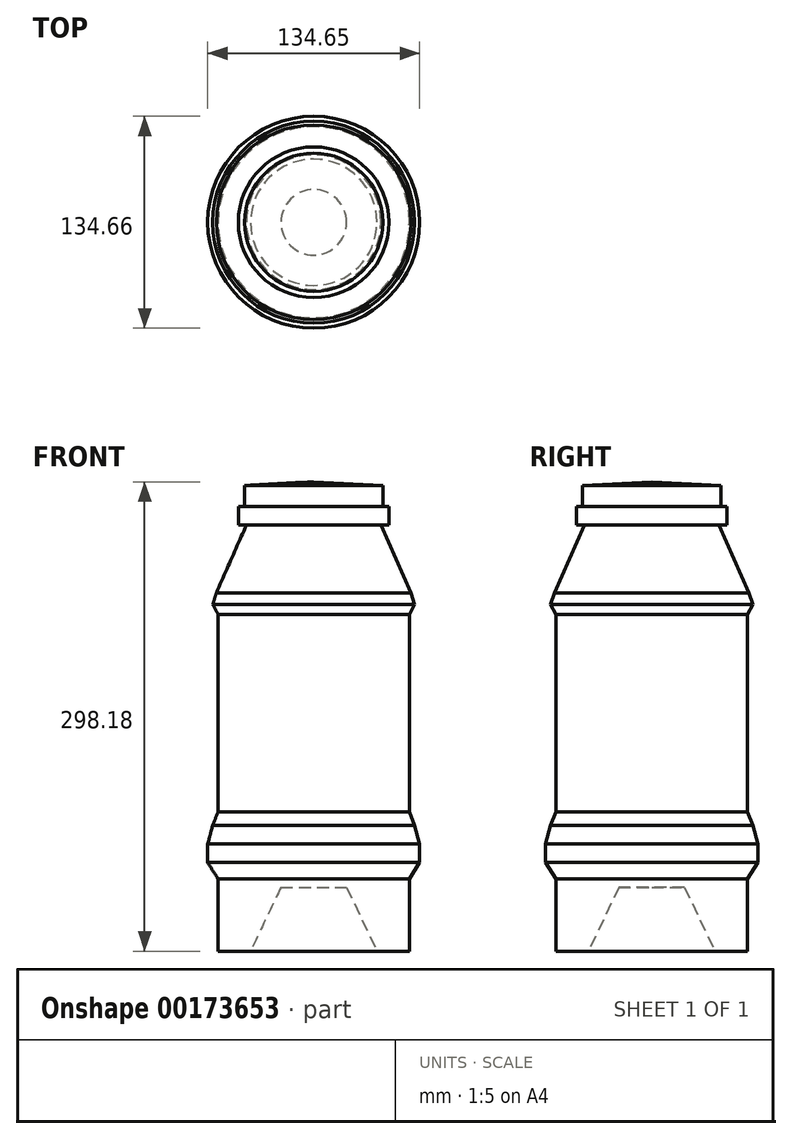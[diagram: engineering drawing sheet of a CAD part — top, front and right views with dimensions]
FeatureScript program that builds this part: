
annotation { "Feature Type Name" : "Feature", "Feature Type Description" : "" }
export const myFeature = defineFeature(function(context is Context, id is Id, definition is map)
    precondition{}
    {
        {
            var Q0;
            Q0=qCreatedBy(makeId("Front.planeOp"),FACE);
            var sketch = newSketch(context, id + "F0", { "sketchPlane" : qUnion([Q0])});
            skLineSegment(sketch, "E0", {"start": v(54.2, 50.63) * mm, "end": v(54.2, 33.8) * mm});
            skLineSegment(sketch, "E1", {"start": v(54.2, 33.8) * mm, "end": v(58.19, 33.8) * mm});
            skLineSegment(sketch, "E2", {"start": v(58.19, 33.8) * mm, "end": v(58.19, 22.1) * mm});
            skLineSegment(sketch, "E3", {"start": v(58.19, 22.1) * mm, "end": v(53.05, 22.1) * mm});
            skLineSegment(sketch, "E4", {"start": v(53.05, 22.1) * mm, "end": v(72.17, -20.97) * mm});
            skLineSegment(sketch, "E5", {"start": v(72.17, -20.97) * mm, "end": v(74.45, -28.38) * mm});
            skLineSegment(sketch, "E6", {"start": v(74.45, -28.38) * mm, "end": v(71.02, -34.66) * mm});
            skLineSegment(sketch, "E7", {"start": v(71.02, -34.66) * mm, "end": v(71.02, -160.02) * mm});
            skLineSegment(sketch, "E8", {"start": v(71.02, -160.02) * mm, "end": v(74.45, -168.64) * mm});
            skLineSegment(sketch, "E9", {"start": v(74.45, -168.64) * mm, "end": v(77.62, -180.5) * mm});
            skLineSegment(sketch, "E10", {"start": v(77.62, -180.5) * mm, "end": v(77.62, -192.36) * mm});
            skLineSegment(sketch, "E11", {"start": v(77.62, -192.36) * mm, "end": v(71.02, -202.79) * mm});
            skLineSegment(sketch, "E12", {"start": v(71.02, -202.79) * mm, "end": v(71.02, -248.67) * mm});
            skLineSegment(sketch, "E13", {"start": v(71.02, -248.67) * mm, "end": v(50.45, -248.67) * mm});
            skLineSegment(sketch, "E14", {"start": v(50.45, -248.67) * mm, "end": v(31.14, -208.01) * mm});
            skLineSegment(sketch, "E15", {"start": v(31.14, -208.01) * mm, "end": v(10.3, -208.01) * mm});
            skLineSegment(sketch, "E16", {"start": v(10.3, -208.01) * mm, "end": v(10.3, 49.5) * mm});
            skLineSegment(sketch, "E17", {"start": v(10.3, 49.5) * mm, "end": v(54.2, 47.2) * mm});
            skSolve(sketch);
        }
        {
            var Q0;
            {var subQ0=sQuery(id+"F0.wireOp",EDGE,"E1");Q0=makeQuery(id+"F0.imprint","IMPRINT",FACE,{"disambiguationData":[TD([[makeQuery(id+"F0.imprint","IMPRINT",EDGE,{"derivedFrom":subQ0}),-1.0]])]});}
            var Q1;
            Q1=sQuery(id+"F0.wireOp",EDGE,"E16");
            revolve(context, id + "F1", {"entities" : qUnion([Q0]), "axis" : qUnion([Q1]), "revolveType" : RevolveType.FULL});
        }
    });
